# Revit family: Farola Solar Olintu S gris
name_source: partatom
category: Luminarias
units: mm (PartAtom-declared; Revit-internal decimal feet)

## family parameters
Compartido = Sí
Corte con vacíos al cargar = No
Cota de conector redondo = Diámetro de uso
Origen de luz = No
Punto de cálculo de habitación = No
Se basa en plano de trabajo = No
Siempre vertical = Sí
Tipo de pieza = Normal

## types (2) — shared parameters
Clase eficiencia energética = A++
Descripción = Farola solar que combina diseño y eficencia
Elevación por defecto = 2000 mm  [stored 6.56168 ft]
Fabricante = Ekiona
Marcado CE = SÍ
Modelo = Modelo Olintu
URL = https://www.ekiona.com
URL producto = https://ekiona.com

## per-type parameters (varying)
| type | Altura columna extremos | Altura columna planos | Descripción de la empresa | Dirección | Distancia brazo-final de columna | Distancia inserto-columa | Gama de acabados | Gama de colores | Garantía | Material columna |
| Farola Olintu S pintura blanca | 4000 mm  [stored 13.1234 ft] | 4000 mm  [stored 13.1234 ft] |  |  | 3500 mm | 3864 mm |  |  | 2 años | <Por categoría> |
| Farola Olintu S pintura gris | 5000 mm  [stored 16.4042 ft] | 5000 mm  [stored 16.4042 ft] | Diseñamos, desarrollamos, fabricamos y comercializamos farolas solares que se adaptan a cualquier necesidad. | Parque Tecnológico Miramón - Paseo Mikeletegi 56 - 20009 Donostia/San Sebastián | 4500 mm | 4864 mm | Galvanizado, Fibra de vidrio, Aluminio | Blanco, Negro, Gris, Verde bosque, acero galvanizado | 5 años | Pintura gris |

note: [stored X ft] marks values corroborated as IEEE doubles in the binary element streams (Revit-internal decimal feet)

## geometry (parser evidence)
native form markers: Blend x6, Sweep x9
no freeform markers — native parametric forms only
